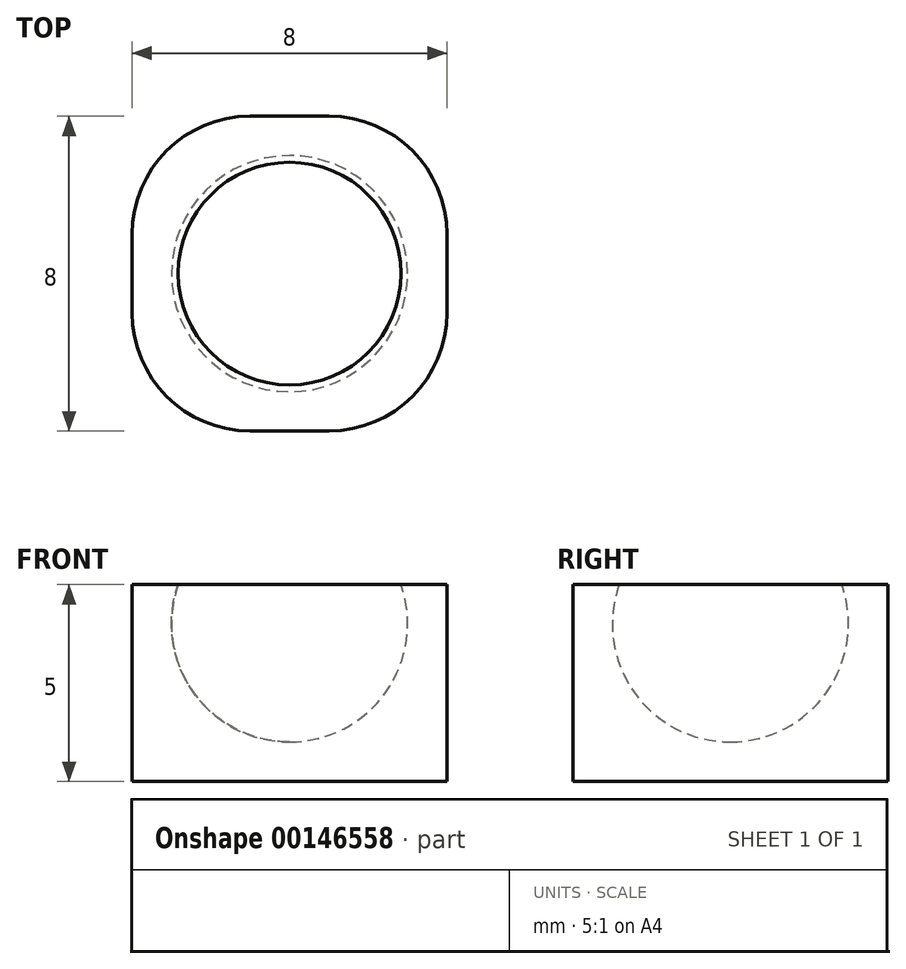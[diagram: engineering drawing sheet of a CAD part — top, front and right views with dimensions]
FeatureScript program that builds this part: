
annotation { "Feature Type Name" : "Feature", "Feature Type Description" : "" }
export const myFeature = defineFeature(function(context is Context, id is Id, definition is map)
    precondition{}
    {
        {
            var Q0;
            Q0=qCreatedBy(makeId("Front.planeOp"),FACE);
            var sketch = newSketch(context, id + "F0", { "sketchPlane" : qUnion([Q0])});
            skLineSegment(sketch, "E0", {"start": v(0, 3.88) * mm, "end": v(0, -3.9) * mm});
            skSolve(sketch);
        }
        {
            var Q0;
            Q0=qCreatedBy(makeId("Front.planeOp"),FACE);
            var sketch = newSketch(context, id + "F1", { "sketchPlane" : qUnion([Q0])});
            skArc(sketch, "E1", {"start": v(-2.83, 5) * mm, "mid": v(-2.45, 2.27) * mm, "end": v(0, 1) * mm});
            skLineSegment(sketch, "E2.bottom", {"start": v(0, 0) * mm, "end": v(-4, 0) * mm});
            skLineSegment(sketch, "E2.top", {"start": v(0, 5) * mm, "end": v(-4, 5) * mm});
            skLineSegment(sketch, "E2.left", {"start": v(0, 0) * mm, "end": v(0, 5) * mm});
            skLineSegment(sketch, "E2.right", {"start": v(-4, 0) * mm, "end": v(-4, 5) * mm});
            skPoint(sketch, "E2.middle", {"position": v(-2, 2.5) * mm});
            skSolve(sketch);
        }
        {
            var Q0;
            {var subQ3=sQuery(id+"F1.wireOp",EDGE,"E2.bottom");Q0=makeQuery(id+"F1.imprint","IMPRINT",FACE,{"disambiguationData":[TD([[makeQuery(id+"F1.imprint","IMPRINT",EDGE,{"derivedFrom":subQ3}),-1.0]])]});}
            var Q1;
            Q1=sQuery(id+"F0.wireOp",EDGE,"E0");
            revolve(context, id + "F2", {"entities" : qUnion([Q0]), "axis" : qUnion([Q1]), "revolveType" : RevolveType.FULL});
        }
        {
            var Q0;
            Q0=qCreatedBy(makeId("Top.planeOp"),FACE);
            var sketch = newSketch(context, id + "F3", { "sketchPlane" : qUnion([Q0])});
            skLineSegment(sketch, "E3.bottom", {"start": v(-4, 4) * mm, "end": v(4, 4) * mm});
            skLineSegment(sketch, "E3.top", {"start": v(-4, -4) * mm, "end": v(4, -4) * mm});
            skLineSegment(sketch, "E3.left", {"start": v(-4, 4) * mm, "end": v(-4, -4) * mm});
            skLineSegment(sketch, "E3.right", {"start": v(4, 4) * mm, "end": v(4, -4) * mm});
            skPoint(sketch, "E3.middle", {"position": v(0, 0) * mm});
            skCircle(sketch, "E4.0.0", {"center": v(0, 0) * mm, "radius": 4 * mm});
            skSolve(sketch);
        }
        {
            var Q0;
            {var subQ0=sQuery(id+"F3.wireOp",EDGE,"E3.left");var subQ1=sQuery(id+"F3.wireOp",EDGE,"E3.top");var subQ2=makeQuery(id+"F3.imprint","INTERSECT",VERTEX,{"derivedFrom":[subQ1,subQ0]});Q0=makeQuery(id+"F3.imprint","IMPRINT",FACE,{"disambiguationData":[TD([[makeQuery(id+"F3.imprint","IMPRINT",EDGE,{"disambiguationData":[TD([[subQ2,-1.0]])],"derivedFrom":subQ1}),1.0]])]});}
            var Q1;
            {var subQ0=sQuery(id+"F3.wireOp",EDGE,"E3.right");var subQ1=sQuery(id+"F3.wireOp",EDGE,"E3.top");var subQ2=makeQuery(id+"F3.imprint","INTERSECT",VERTEX,{"derivedFrom":[subQ1,subQ0]});Q1=makeQuery(id+"F3.imprint","IMPRINT",FACE,{"disambiguationData":[TD([[makeQuery(id+"F3.imprint","IMPRINT",EDGE,{"disambiguationData":[TD([[subQ2,1.0]])],"derivedFrom":subQ1}),1.0]])]});}
            var Q2;
            {var subQ0=sQuery(id+"F3.wireOp",EDGE,"E3.right");var subQ1=sQuery(id+"F3.wireOp",EDGE,"E3.bottom");var subQ2=makeQuery(id+"F3.imprint","INTERSECT",VERTEX,{"derivedFrom":[subQ1,subQ0]});Q2=makeQuery(id+"F3.imprint","IMPRINT",FACE,{"disambiguationData":[TD([[makeQuery(id+"F3.imprint","IMPRINT",EDGE,{"disambiguationData":[TD([[subQ2,1.0]])],"derivedFrom":subQ1}),-1.0]])]});}
            var Q3;
            {var subQ0=sQuery(id+"F3.wireOp",EDGE,"E3.left");var subQ1=sQuery(id+"F3.wireOp",EDGE,"E3.bottom");var subQ2=makeQuery(id+"F3.imprint","INTERSECT",VERTEX,{"derivedFrom":[subQ1,subQ0]});Q3=makeQuery(id+"F3.imprint","IMPRINT",FACE,{"disambiguationData":[TD([[makeQuery(id+"F3.imprint","IMPRINT",EDGE,{"disambiguationData":[TD([[subQ2,-1.0]])],"derivedFrom":subQ1}),-1.0]])]});}
            extrude(context, id + "F4", {"entities" : qUnion([Q0, Q1, Q2, Q3]), "operationType" : NewBodyOperationType.ADD, "depth" : 5 * mm});
        }
        {
            var Q0;
            Q0=makeQuery(id+"F4.opExtrude","SWEPT_EDGE",EDGE,{"disambiguationData":[OSD([sQuery(id+"F3.wireOp",EDGE,"E3.top"),sQuery(id+"F3.wireOp",EDGE,"E3.right")])]});
            var Q1;
            Q1=makeQuery(id+"F4.opExtrude","SWEPT_EDGE",EDGE,{"disambiguationData":[OSD([sQuery(id+"F3.wireOp",EDGE,"E3.bottom"),sQuery(id+"F3.wireOp",EDGE,"E3.right")])]});
            var Q2;
            Q2=makeQuery(id+"F4.opExtrude","SWEPT_EDGE",EDGE,{"disambiguationData":[OSD([sQuery(id+"F3.wireOp",EDGE,"E3.top"),sQuery(id+"F3.wireOp",EDGE,"E3.left")])]});
            var Q3;
            Q3=makeQuery(id+"F4.opExtrude","SWEPT_EDGE",EDGE,{"disambiguationData":[OSD([sQuery(id+"F3.wireOp",EDGE,"E3.bottom"),sQuery(id+"F3.wireOp",EDGE,"E3.left")])]});
            fillet(context, id + "F5", {"entities" : qUnion([Q0, Q1, Q2, Q3]), "radius" : 3 * mm, "tangentPropagation" : true, "allowEdgeOverflow" : false});
        }
    });
